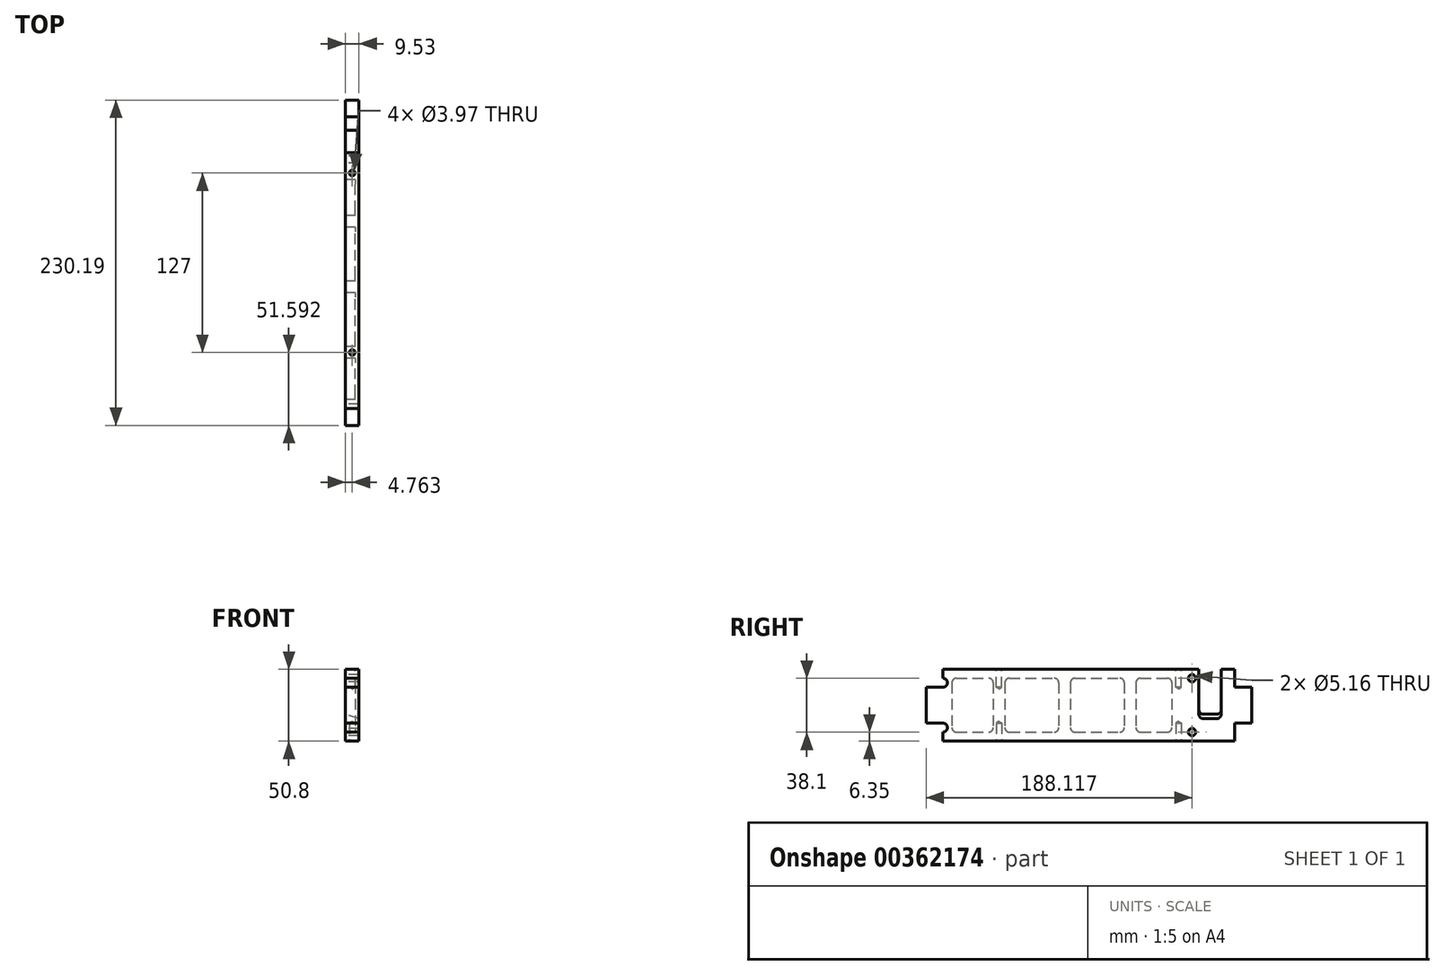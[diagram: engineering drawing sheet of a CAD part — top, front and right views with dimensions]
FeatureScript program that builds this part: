
annotation { "Feature Type Name" : "Feature", "Feature Type Description" : "" }
export const myFeature = defineFeature(function(context is Context, id is Id, definition is map)
    precondition{}
    {
        {
            var Q0;
            Q0=qCreatedBy(makeId("Right.planeOp"),FACE);
            var sketch = newSketch(context, id + "F0", { "sketchPlane" : qUnion([Q0])});
            skLineSegment(sketch, "E0", {"start": v(-255.12, 0) * mm, "end": v(-190.37, 0) * mm, "construction": true});
            skLineSegment(sketch, "E1", {"start": v(-178.47, -12.7) * mm, "end": v(27.9, -12.7) * mm});
            skLineSegment(sketch, "E2", {"start": v(104.57, 0) * mm, "end": v(83.25, 25.4) * mm, "construction": true});
            skLineSegment(sketch, "E3", {"start": v(83.25, 25.4) * mm, "end": v(39.82, 25.4) * mm, "construction": true});
            skLineSegment(sketch, "E4", {"start": v(2.5, 38.1) * mm, "end": v(-178.47, 38.1) * mm});
            skLineSegment(sketch, "E5", {"start": v(-178.47, 38.1) * mm, "end": v(-178.47, 31.75) * mm});
            skLineSegment(sketch, "E6", {"start": v(-190.37, 25.4) * mm, "end": v(-233.8, 25.4) * mm, "construction": true});
            skLineSegment(sketch, "E7", {"start": v(-233.8, 25.4) * mm, "end": v(-255.12, 0) * mm, "construction": true});
            skLineSegment(sketch, "E8", {"start": v(-178.47, -12.7) * mm, "end": v(-265.78, -12.7) * mm, "construction": true});
            skLineSegment(sketch, "E9", {"start": v(-265.78, -12.7) * mm, "end": v(-255.12, 0) * mm, "construction": true});
            skLineSegment(sketch, "E10", {"start": v(27.9, -12.7) * mm, "end": v(115.22, -12.7) * mm, "construction": true});
            skLineSegment(sketch, "E11", {"start": v(115.22, -12.7) * mm, "end": v(104.57, 0) * mm, "construction": true});
            skLineSegment(sketch, "E12", {"start": v(2.5, 38.1) * mm, "end": v(2.5, 6.35) * mm});
            skLineSegment(sketch, "E13", {"start": v(-7.02, -12.7) * mm, "end": v(-7.02, 38.1) * mm, "construction": true});
            skLineSegment(sketch, "E14", {"start": v(2.5, 0) * mm, "end": v(-7.02, 0) * mm, "construction": true});
            skLineSegment(sketch, "E15", {"start": v(2.5, 25.4) * mm, "end": v(-7.02, 25.4) * mm, "construction": true});
            skLineSegment(sketch, "E16", {"start": v(-2.25, 25.4) * mm, "end": v(-2.25, 38.1) * mm, "construction": true});
            skLineSegment(sketch, "E17", {"start": v(-2.25, 0) * mm, "end": v(-2.25, -12.7) * mm, "construction": true});
            skPoint(sketch, "E18", {"position": v(-2.25, 25.4) * mm});
            skPoint(sketch, "E19", {"position": v(-2.25, 0) * mm});
            skLineSegment(sketch, "E20", {"start": v(-2.25, 0) * mm, "end": v(-2.25, 12.7) * mm, "construction": true});
            skLineSegment(sketch, "E21", {"start": v(-2.25, 12.7) * mm, "end": v(-2.25, 25.4) * mm, "construction": true});
            skPoint(sketch, "E22", {"position": v(-2.25, 12.7) * mm});
            skLineSegment(sketch, "E23", {"start": v(2.5, 0) * mm, "end": v(2.5, -12.7) * mm, "construction": true});
            skLineSegment(sketch, "E24", {"start": v(2.5, 0) * mm, "end": v(2.5, 12.24) * mm, "construction": true});
            skLineSegment(sketch, "E25", {"start": v(2.5, 6.35) * mm, "end": v(2.5, 12.24) * mm});
            skArc(sketch, "E26", {"start": v(-178.47, -6.35) * mm, "mid": v(-175.3, -3.18) * mm, "end": v(-178.47, 0) * mm});
            skLineSegment(sketch, "E27.trimOffspring", {"start": v(-178.47, -6.35) * mm, "end": v(-178.47, -12.7) * mm});
            skArc(sketch, "E28", {"start": v(-178.47, 25.4) * mm, "mid": v(-175.3, 28.58) * mm, "end": v(-178.47, 31.75) * mm});
            skLineSegment(sketch, "E29", {"start": v(-178.47, 31.75) * mm, "end": v(-178.47, 28.57) * mm, "construction": true});
            skLineSegment(sketch, "E30", {"start": v(-178.47, 25.4) * mm, "end": v(-178.47, 28.57) * mm, "construction": true});
            skLineSegment(sketch, "E31", {"start": v(-178.47, -6.35) * mm, "end": v(-178.47, -3.18) * mm, "construction": true});
            skLineSegment(sketch, "E32", {"start": v(-178.47, -3.18) * mm, "end": v(-178.47, 0) * mm, "construction": true});
            skPoint(sketch, "E33", {"position": v(-2.25, 31.75) * mm});
            skPoint(sketch, "E34", {"position": v(-2.25, -6.35) * mm});
            skLineSegment(sketch, "E35", {"start": v(18.38, 38.1) * mm, "end": v(27.9, 38.1) * mm});
            skLineSegment(sketch, "E36", {"start": v(27.9, 38.1) * mm, "end": v(27.9, 25.4) * mm});
            skLineSegment(sketch, "E37", {"start": v(18.38, 38.1) * mm, "end": v(2.5, 38.1) * mm, "construction": true});
            skLineSegment(sketch, "E38", {"start": v(27.9, -12.7) * mm, "end": v(27.9, 0) * mm});
            skLineSegment(sketch, "E39", {"start": v(18.38, 38.1) * mm, "end": v(18.38, 6.35) * mm});
            skLineSegment(sketch, "E40", {"start": v(18.38, 6.35) * mm, "end": v(2.5, 6.35) * mm});
            skLineSegment(sketch, "E41", {"start": v(39.82, 0) * mm, "end": v(104.57, 0) * mm, "construction": true});
            skLineSegment(sketch, "E42", {"start": v(27.9, 25.4) * mm, "end": v(27.9, 0) * mm, "construction": true});
            skLineSegment(sketch, "E43", {"start": v(-190.37, 25.4) * mm, "end": v(-190.37, 0) * mm});
            skLineSegment(sketch, "E44", {"start": v(-178.47, 25.4) * mm, "end": v(-190.37, 25.4) * mm});
            skLineSegment(sketch, "E45", {"start": v(-178.47, 0) * mm, "end": v(-190.37, 0) * mm});
            skLineSegment(sketch, "E46", {"start": v(39.82, 25.4) * mm, "end": v(39.82, 0) * mm});
            skLineSegment(sketch, "E47", {"start": v(39.82, 25.4) * mm, "end": v(27.9, 25.4) * mm});
            skLineSegment(sketch, "E48", {"start": v(39.82, 0) * mm, "end": v(27.9, 0) * mm});
            skLineSegment(sketch, "E49.bottom", {"start": v(-172.12, 31.75) * mm, "end": v(-142.9, 31.75) * mm});
            skLineSegment(sketch, "E49.top", {"start": v(-172.12, -6.35) * mm, "end": v(-142.9, -6.35) * mm});
            skLineSegment(sketch, "E49.left", {"start": v(-172.12, 31.75) * mm, "end": v(-172.12, -6.35) * mm});
            skLineSegment(sketch, "E49.right", {"start": v(-142.9, 31.75) * mm, "end": v(-142.9, -6.35) * mm});
            skLineSegment(sketch, "E50.bottom", {"start": v(-134.65, 31.75) * mm, "end": v(-96.55, 31.75) * mm});
            skLineSegment(sketch, "E50.top", {"start": v(-134.65, -6.35) * mm, "end": v(-96.55, -6.35) * mm});
            skLineSegment(sketch, "E50.left", {"start": v(-134.65, 31.75) * mm, "end": v(-134.65, -6.35) * mm});
            skLineSegment(sketch, "E50.right", {"start": v(-96.55, 31.75) * mm, "end": v(-96.55, -6.35) * mm});
            skLineSegment(sketch, "E51.bottom", {"start": v(-88.3, 31.75) * mm, "end": v(-50.2, 31.75) * mm});
            skLineSegment(sketch, "E51.top", {"start": v(-88.3, -6.35) * mm, "end": v(-50.2, -6.35) * mm});
            skLineSegment(sketch, "E51.left", {"start": v(-88.3, 31.75) * mm, "end": v(-88.3, -6.35) * mm});
            skLineSegment(sketch, "E51.right", {"start": v(-50.2, 31.75) * mm, "end": v(-50.2, -6.35) * mm});
            skLineSegment(sketch, "E52", {"start": v(-172.12, 31.75) * mm, "end": v(-172.12, 38.1) * mm, "construction": true});
            skLineSegment(sketch, "E53", {"start": v(-142.9, 31.75) * mm, "end": v(-134.65, 31.75) * mm, "construction": true});
            skLineSegment(sketch, "E54", {"start": v(-96.55, 31.75) * mm, "end": v(-88.3, 31.75) * mm, "construction": true});
            skLineSegment(sketch, "E55", {"start": v(-172.12, -6.35) * mm, "end": v(-172.12, -12.7) * mm, "construction": true});
            skLineSegment(sketch, "E56.bottom", {"start": v(-41.94, 31.75) * mm, "end": v(-16.54, 31.75) * mm});
            skLineSegment(sketch, "E56.top", {"start": v(-41.94, -6.35) * mm, "end": v(-16.54, -6.35) * mm});
            skLineSegment(sketch, "E56.left", {"start": v(-41.94, 31.75) * mm, "end": v(-41.94, -6.35) * mm});
            skLineSegment(sketch, "E56.right", {"start": v(-16.54, 31.75) * mm, "end": v(-16.54, -6.35) * mm});
            skLineSegment(sketch, "E57", {"start": v(-50.2, 31.75) * mm, "end": v(-41.94, 31.75) * mm, "construction": true});
            skSolve(sketch);
        }
        {
            var Q0;
            Q0 = qSketchRegion(id + "F0", true);
            var Q1;
            Q1=makeQuery(id+"F0.imprint","IMPRINT",FACE,{"disambiguationData":[TD([[makeQuery(id+"F0.imprint","IMPRINT",EDGE,{"derivedFrom":sQuery(id+"F0.wireOp",EDGE,"E49.bottom")}),-1.0]])]});
            var Q2;
            Q2=makeQuery(id+"F0.imprint","IMPRINT",FACE,{"disambiguationData":[TD([[makeQuery(id+"F0.imprint","IMPRINT",EDGE,{"derivedFrom":sQuery(id+"F0.wireOp",EDGE,"E50.bottom")}),-1.0]])]});
            var Q3;
            Q3=makeQuery(id+"F0.imprint","IMPRINT",FACE,{"disambiguationData":[TD([[makeQuery(id+"F0.imprint","IMPRINT",EDGE,{"derivedFrom":sQuery(id+"F0.wireOp",EDGE,"E51.bottom")}),-1.0]])]});
            var Q4;
            Q4=makeQuery(id+"F0.imprint","IMPRINT",FACE,{"disambiguationData":[TD([[makeQuery(id+"F0.imprint","IMPRINT",EDGE,{"derivedFrom":sQuery(id+"F0.wireOp",EDGE,"E56.bottom")}),-1.0]])]});
            extrude(context, id + "F1", {"entities" : qUnion([Q0, Q1, Q2, Q3, Q4]), "depth" : 9.52 * mm, "offsetDistance" : 25.4 * mm});
        }
        {
            var Q0;
            Q0=sQuery(id+"F0.wireOp",VERTEX,"E33");
            var Q1;
            Q1=sQuery(id+"F0.wireOp",VERTEX,"E34");
            var Q2;
            Q2=makeQuery(id+"F1.opExtrude","SWEPT_BODY",BODY,{"disambiguationData":[OSD([sQuery(id+"F0.wireOp",EDGE,"E0"),sQuery(id+"F0.wireOp",EDGE,"9FReQoBW-hrfJ-Pff4-7W1h-hT4dUridyVJD"),sQuery(id+"F0.wireOp",EDGE,"E1"),sQuery(id+"F0.wireOp",EDGE,"JQ5G8gi4-YxyZ-LOKj-CqmL-p0KQ2LY8LaAz"),sQuery(id+"F0.wireOp",EDGE,"kSwPHoP6-dxIY-U89x-ailE-mJDE5nYmn2aF"),sQuery(id+"F0.wireOp",EDGE,"E2"),sQuery(id+"F0.wireOp",EDGE,"E3"),sQuery(id+"F0.wireOp",EDGE,"E4"),sQuery(id+"F0.wireOp",EDGE,"E5"),sQuery(id+"F0.wireOp",EDGE,"E6"),sQuery(id+"F0.wireOp",EDGE,"E7"),sQuery(id+"F0.wireOp",EDGE,"E12"),sQuery(id+"F0.wireOp",EDGE,"xUa2it0l-wrGz-603z-r9Vx-WFFZ9Qz045jS")])]});
            hole(context, id + "F2", {"style" : HoleStyle.SIMPLE, "endStyle" : HoleEndStyle.THROUGH, "oppositeDirection" : true, "holeDiameter" : 5.16 * mm, "isTappedThrough" : true, "tappedDepth" : 12.7 * mm, "tapClearance" : 3, "startFromSketch" : true, "locations" : qUnion([Q0, Q1]), "scope" : qUnion([Q2])});
        }
        {
            var Q0;
            Q0=makeQuery(id+"F1.opExtrude","CAP_EDGE",EDGE,{"disambiguationData":[OSD([sQuery(id+"F0.wireOp",EDGE,"FVBeHJ3c-TPnr-ykfa-VAbP-4ejNwkg1UkDG")])],"isStart":false});
            var Q1;
            Q1=makeQuery(id+"F1.opExtrude","CAP_EDGE",EDGE,{"disambiguationData":[OSD([sQuery(id+"F0.wireOp",EDGE,"E40")])],"isStart":false});
            chamfer(context, id + "F3", {"entities" : qUnion([Q0, Q1]), "chamferType" : ChamferType.TWO_OFFSETS, "width1" : 3.17 * mm, "oppositeDirection" : false, "width2" : 9.52 * mm, "tangentPropagation" : true});
        }
        {
            var Q0;
            Q0=makeQuery(id+"F3.opChamfer","BLEND_EDGE",EDGE,{"blendedFrom":[makeQuery(id+"F1.opExtrude","CAP_EDGE",EDGE,{"disambiguationData":[OSD([sQuery(id+"F0.wireOp",EDGE,"E40")])],"isStart":false}),makeQuery(id+"F1.opExtrude","SWEPT_FACE",FACE,{"disambiguationData":[OSD([sQuery(id+"F0.wireOp",EDGE,"E39")])]})],"blendedInto":[makeQuery(id+"F1.opExtrude","SWEPT_FACE",FACE,{"disambiguationData":[OSD([sQuery(id+"F0.wireOp",EDGE,"E39")])]})]});
            var Q1;
            Q1=makeQuery(id+"F3.opChamfer","BLEND_EDGE",EDGE,{"blendedFrom":[makeQuery(id+"F1.opExtrude","CAP_EDGE",EDGE,{"disambiguationData":[OSD([sQuery(id+"F0.wireOp",EDGE,"E40")])],"isStart":false}),makeQuery(id+"F1.opExtrude","SWEPT_FACE",FACE,{"disambiguationData":[OSD([sQuery(id+"F0.wireOp",EDGE,"E12"),sQuery(id+"F0.wireOp",EDGE,"E25")])]})],"blendedInto":[makeQuery(id+"F1.opExtrude","SWEPT_FACE",FACE,{"disambiguationData":[OSD([sQuery(id+"F0.wireOp",EDGE,"E12"),sQuery(id+"F0.wireOp",EDGE,"E25")])]})]});
            fillet(context, id + "F4", {"entities" : qUnion([Q0, Q1]), "radius" : 3.17 * mm, "tangentPropagation" : true, "allowEdgeOverflow" : false});
        }
        {
            var Q0;
            Q0=makeQuery(id+"F1.opExtrude","SWEPT_FACE",FACE,{"disambiguationData":[OSD([sQuery(id+"F0.wireOp",EDGE,"E4")])]});
            var sketch = newSketch(context, id + "F5", { "sketchPlane" : qUnion([Q0])});
            skPoint(sketch, "E58.0", {"position": v(4.76, -178.47) * mm});
            skPoint(sketch, "E59.0", {"position": v(4.76, 2.5) * mm});
            skLineSegment(sketch, "E60", {"start": v(4.76, -178.47) * mm, "end": v(4.76, -138.78) * mm, "construction": true});
            skPoint(sketch, "E61", {"position": v(4.76, -138.78) * mm});
            skLineSegment(sketch, "E62", {"start": v(4.76, -138.78) * mm, "end": v(4.76, -11.78) * mm, "construction": true});
            skPoint(sketch, "E63", {"position": v(4.76, -11.78) * mm});
            skPoint(sketch, "E64.0", {"position": v(4.76, 27.9) * mm});
            skLineSegment(sketch, "E65", {"start": v(4.76, -11.78) * mm, "end": v(4.76, 27.9) * mm, "construction": true});
            skSolve(sketch);
        }
        {
            var Q0;
            Q0=sQuery(id+"F5.wireOp",VERTEX,"E61");
            var Q1;
            Q1=sQuery(id+"F5.wireOp",VERTEX,"E63");
            var Q2;
            Q2=makeQuery(id+"F1.opExtrude","SWEPT_BODY",BODY,{"disambiguationData":[OSD([sQuery(id+"F0.wireOp",EDGE,"E0"),sQuery(id+"F0.wireOp",EDGE,"E1"),sQuery(id+"F0.wireOp",EDGE,"E2"),sQuery(id+"F0.wireOp",EDGE,"E3"),sQuery(id+"F0.wireOp",EDGE,"E4"),sQuery(id+"F0.wireOp",EDGE,"E5"),sQuery(id+"F0.wireOp",EDGE,"E6"),sQuery(id+"F0.wireOp",EDGE,"E7"),sQuery(id+"F0.wireOp",EDGE,"E12"),sQuery(id+"F0.wireOp",EDGE,"E25"),sQuery(id+"F0.wireOp",EDGE,"E26"),sQuery(id+"F0.wireOp",EDGE,"E27.trimOffspring"),sQuery(id+"F0.wireOp",EDGE,"E28"),sQuery(id+"F0.wireOp",EDGE,"E35"),sQuery(id+"F0.wireOp",EDGE,"E36"),sQuery(id+"F0.wireOp",EDGE,"E38"),sQuery(id+"F0.wireOp",EDGE,"E39"),sQuery(id+"F0.wireOp",EDGE,"E40"),sQuery(id+"F0.wireOp",EDGE,"E41")])]});
            hole(context, id + "F6", {"style" : HoleStyle.SIMPLE, "endStyle" : HoleEndStyle.BLIND, "holeDiameter" : 3.97 * mm, "holeDepth" : 12.7 * mm, "isTappedThrough" : true, "tappedDepth" : 12.7 * mm, "tapClearance" : 3, "startFromSketch" : true, "locations" : qUnion([Q0, Q1]), "scope" : qUnion([Q2])});
        }
        {
            var Q0;
            Q0=makeQuery(id+"F1.opExtrude","SWEPT_FACE",FACE,{"disambiguationData":[OSD([sQuery(id+"F0.wireOp",EDGE,"E1")])]});
            var sketch = newSketch(context, id + "F7", { "sketchPlane" : qUnion([Q0])});
            skPoint(sketch, "E66.0", {"position": v(0, 178.47) * mm});
            skPoint(sketch, "E67.0", {"position": v(4.76, -27.9) * mm});
            skLineSegment(sketch, "E68", {"start": v(4.76, 178.47) * mm, "end": v(4.76, 138.78) * mm, "construction": true});
            skPoint(sketch, "E69", {"position": v(4.76, 138.78) * mm});
            skLineSegment(sketch, "E70", {"start": v(4.76, 138.78) * mm, "end": v(4.76, 11.78) * mm, "construction": true});
            skPoint(sketch, "E71", {"position": v(4.76, 11.78) * mm});
            skLineSegment(sketch, "E72", {"start": v(4.76, 11.78) * mm, "end": v(4.76, -27.9) * mm, "construction": true});
            skSolve(sketch);
        }
        {
            var Q0;
            Q0=sQuery(id+"F7.wireOp",VERTEX,"E69");
            var Q1;
            Q1=sQuery(id+"F7.wireOp",VERTEX,"E71");
            var Q2;
            Q2=makeQuery(id+"F1.opExtrude","SWEPT_BODY",BODY,{"disambiguationData":[OSD([sQuery(id+"F0.wireOp",EDGE,"E0"),sQuery(id+"F0.wireOp",EDGE,"E1"),sQuery(id+"F0.wireOp",EDGE,"E2"),sQuery(id+"F0.wireOp",EDGE,"E3"),sQuery(id+"F0.wireOp",EDGE,"E4"),sQuery(id+"F0.wireOp",EDGE,"E5"),sQuery(id+"F0.wireOp",EDGE,"E6"),sQuery(id+"F0.wireOp",EDGE,"E7"),sQuery(id+"F0.wireOp",EDGE,"E12"),sQuery(id+"F0.wireOp",EDGE,"E25"),sQuery(id+"F0.wireOp",EDGE,"E26"),sQuery(id+"F0.wireOp",EDGE,"E27.trimOffspring"),sQuery(id+"F0.wireOp",EDGE,"E28"),sQuery(id+"F0.wireOp",EDGE,"E35"),sQuery(id+"F0.wireOp",EDGE,"E36"),sQuery(id+"F0.wireOp",EDGE,"E38"),sQuery(id+"F0.wireOp",EDGE,"E39"),sQuery(id+"F0.wireOp",EDGE,"E40"),sQuery(id+"F0.wireOp",EDGE,"E41")])]});
            hole(context, id + "F8", {"style" : HoleStyle.SIMPLE, "endStyle" : HoleEndStyle.BLIND, "holeDiameter" : 3.97 * mm, "holeDepth" : 12.7 * mm, "isTappedThrough" : true, "tappedDepth" : 12.7 * mm, "tapClearance" : 3, "startFromSketch" : true, "locations" : qUnion([Q0, Q1]), "scope" : qUnion([Q2])});
        }
        {
            var Q0;
            Q0=makeQuery(id+"F0.imprint","IMPRINT",FACE,{"disambiguationData":[TD([[makeQuery(id+"F0.imprint","IMPRINT",EDGE,{"derivedFrom":sQuery(id+"F0.wireOp",EDGE,"E56.bottom")}),-1.0]])]});
            var Q1;
            Q1=makeQuery(id+"F0.imprint","IMPRINT",FACE,{"disambiguationData":[TD([[makeQuery(id+"F0.imprint","IMPRINT",EDGE,{"derivedFrom":sQuery(id+"F0.wireOp",EDGE,"E51.bottom")}),-1.0]])]});
            var Q2;
            Q2=makeQuery(id+"F0.imprint","IMPRINT",FACE,{"disambiguationData":[TD([[makeQuery(id+"F0.imprint","IMPRINT",EDGE,{"derivedFrom":sQuery(id+"F0.wireOp",EDGE,"E50.bottom")}),-1.0]])]});
            var Q3;
            Q3=makeQuery(id+"F0.imprint","IMPRINT",FACE,{"disambiguationData":[TD([[makeQuery(id+"F0.imprint","IMPRINT",EDGE,{"derivedFrom":sQuery(id+"F0.wireOp",EDGE,"E49.bottom")}),-1.0]])]});
            extrude(context, id + "F9", {"entities" : qUnion([Q0, Q1, Q2, Q3]), "operationType" : NewBodyOperationType.REMOVE, "depth" : 7 * mm, "offsetDistance" : 25.4 * mm});
        }
        {
            var Q0;
            Q0=makeQuery(id+"F9.boolean.opBoolean","COPY",EDGE,{"derivedFrom":makeQuery(id+"F9.opExtrude","SWEPT_EDGE",EDGE,{"disambiguationData":[OSD([sQuery(id+"F0.wireOp",EDGE,"E56.bottom"),sQuery(id+"F0.wireOp",EDGE,"E56.right")])]})});
            var Q1;
            Q1=makeQuery(id+"F9.boolean.opBoolean","COPY",EDGE,{"derivedFrom":makeQuery(id+"F9.opExtrude","SWEPT_EDGE",EDGE,{"disambiguationData":[OSD([sQuery(id+"F0.wireOp",EDGE,"E51.bottom"),sQuery(id+"F0.wireOp",EDGE,"E51.right")])]})});
            var Q2;
            Q2=makeQuery(id+"F9.boolean.opBoolean","COPY",EDGE,{"derivedFrom":makeQuery(id+"F9.opExtrude","SWEPT_EDGE",EDGE,{"disambiguationData":[OSD([sQuery(id+"F0.wireOp",EDGE,"E50.bottom"),sQuery(id+"F0.wireOp",EDGE,"E50.right")])]})});
            var Q3;
            Q3=makeQuery(id+"F9.boolean.opBoolean","COPY",EDGE,{"derivedFrom":makeQuery(id+"F9.opExtrude","SWEPT_EDGE",EDGE,{"disambiguationData":[OSD([sQuery(id+"F0.wireOp",EDGE,"E49.bottom"),sQuery(id+"F0.wireOp",EDGE,"E49.right")])]})});
            var Q4;
            Q4=makeQuery(id+"F9.boolean.opBoolean","COPY",EDGE,{"derivedFrom":makeQuery(id+"F9.opExtrude","SWEPT_EDGE",EDGE,{"disambiguationData":[OSD([sQuery(id+"F0.wireOp",EDGE,"E49.bottom"),sQuery(id+"F0.wireOp",EDGE,"E49.left")])]})});
            var Q5;
            Q5=makeQuery(id+"F9.boolean.opBoolean","COPY",EDGE,{"derivedFrom":makeQuery(id+"F9.opExtrude","SWEPT_EDGE",EDGE,{"disambiguationData":[OSD([sQuery(id+"F0.wireOp",EDGE,"E50.bottom"),sQuery(id+"F0.wireOp",EDGE,"E50.left")])]})});
            var Q6;
            Q6=makeQuery(id+"F9.boolean.opBoolean","COPY",EDGE,{"derivedFrom":makeQuery(id+"F9.opExtrude","SWEPT_EDGE",EDGE,{"disambiguationData":[OSD([sQuery(id+"F0.wireOp",EDGE,"E51.bottom"),sQuery(id+"F0.wireOp",EDGE,"E51.left")])]})});
            var Q7;
            Q7=makeQuery(id+"F9.boolean.opBoolean","COPY",EDGE,{"derivedFrom":makeQuery(id+"F9.opExtrude","SWEPT_EDGE",EDGE,{"disambiguationData":[OSD([sQuery(id+"F0.wireOp",EDGE,"E56.bottom"),sQuery(id+"F0.wireOp",EDGE,"E56.left")])]})});
            var Q8;
            Q8=makeQuery(id+"F9.boolean.opBoolean","COPY",EDGE,{"derivedFrom":makeQuery(id+"F9.opExtrude","SWEPT_EDGE",EDGE,{"disambiguationData":[OSD([sQuery(id+"F0.wireOp",EDGE,"E56.top"),sQuery(id+"F0.wireOp",EDGE,"E56.right")])]})});
            var Q9;
            Q9=makeQuery(id+"F9.boolean.opBoolean","COPY",EDGE,{"derivedFrom":makeQuery(id+"F9.opExtrude","SWEPT_EDGE",EDGE,{"disambiguationData":[OSD([sQuery(id+"F0.wireOp",EDGE,"E51.top"),sQuery(id+"F0.wireOp",EDGE,"E51.right")])]})});
            var Q10;
            Q10=makeQuery(id+"F9.boolean.opBoolean","COPY",EDGE,{"derivedFrom":makeQuery(id+"F9.opExtrude","SWEPT_EDGE",EDGE,{"disambiguationData":[OSD([sQuery(id+"F0.wireOp",EDGE,"E50.top"),sQuery(id+"F0.wireOp",EDGE,"E50.right")])]})});
            var Q11;
            Q11=makeQuery(id+"F9.boolean.opBoolean","COPY",EDGE,{"derivedFrom":makeQuery(id+"F9.opExtrude","SWEPT_EDGE",EDGE,{"disambiguationData":[OSD([sQuery(id+"F0.wireOp",EDGE,"E49.top"),sQuery(id+"F0.wireOp",EDGE,"E49.right")])]})});
            var Q12;
            Q12=makeQuery(id+"F9.boolean.opBoolean","COPY",EDGE,{"derivedFrom":makeQuery(id+"F9.opExtrude","SWEPT_EDGE",EDGE,{"disambiguationData":[OSD([sQuery(id+"F0.wireOp",EDGE,"E56.top"),sQuery(id+"F0.wireOp",EDGE,"E56.left")])]})});
            var Q13;
            Q13=makeQuery(id+"F9.boolean.opBoolean","COPY",EDGE,{"derivedFrom":makeQuery(id+"F9.opExtrude","SWEPT_EDGE",EDGE,{"disambiguationData":[OSD([sQuery(id+"F0.wireOp",EDGE,"E51.top"),sQuery(id+"F0.wireOp",EDGE,"E51.left")])]})});
            var Q14;
            Q14=makeQuery(id+"F9.boolean.opBoolean","COPY",EDGE,{"derivedFrom":makeQuery(id+"F9.opExtrude","SWEPT_EDGE",EDGE,{"disambiguationData":[OSD([sQuery(id+"F0.wireOp",EDGE,"E50.top"),sQuery(id+"F0.wireOp",EDGE,"E50.left")])]})});
            var Q15;
            Q15=makeQuery(id+"F9.boolean.opBoolean","COPY",EDGE,{"derivedFrom":makeQuery(id+"F9.opExtrude","SWEPT_EDGE",EDGE,{"disambiguationData":[OSD([sQuery(id+"F0.wireOp",EDGE,"E49.top"),sQuery(id+"F0.wireOp",EDGE,"E49.left")])]})});
            fillet(context, id + "F10", {"entities" : qUnion([Q0, Q1, Q2, Q3, Q4, Q5, Q6, Q7, Q8, Q9, Q10, Q11, Q12, Q13, Q14, Q15]), "radius" : 3.17 * mm, "tangentPropagation" : true, "allowEdgeOverflow" : false});
        }
    });
